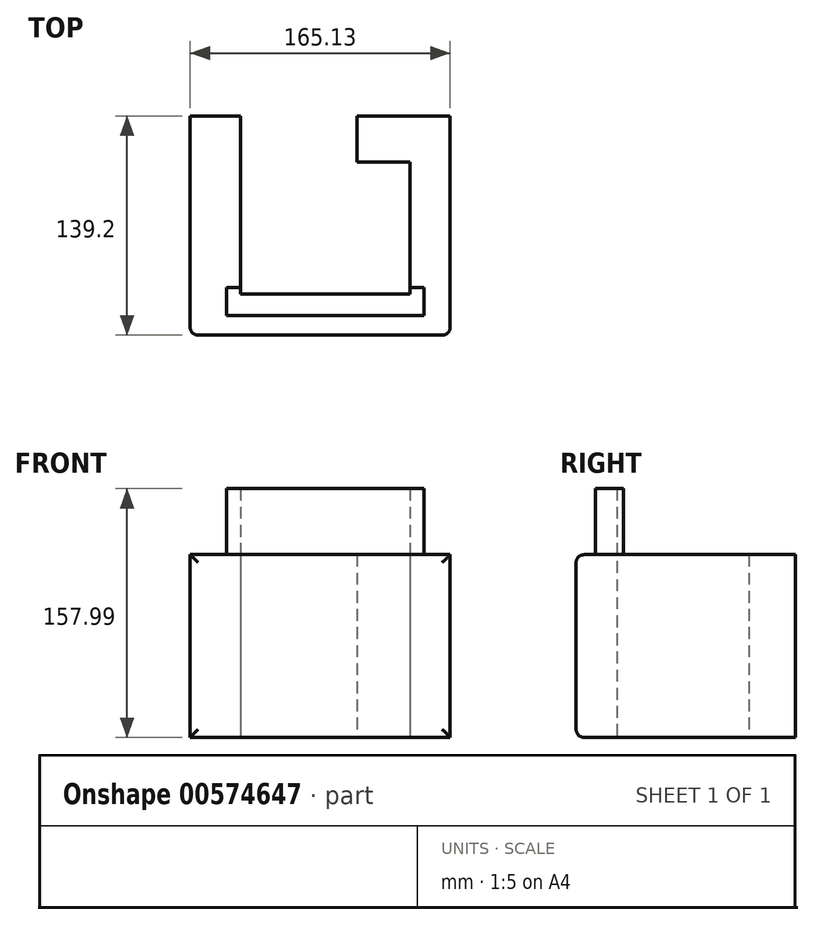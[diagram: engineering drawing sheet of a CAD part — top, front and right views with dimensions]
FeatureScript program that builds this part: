
annotation { "Feature Type Name" : "Feature", "Feature Type Description" : "" }
export const myFeature = defineFeature(function(context is Context, id is Id, definition is map)
    precondition{}
    {
        {
            var Q0;
            Q0=qCreatedBy(makeId("Top.planeOp"),FACE);
            var sketch = newSketch(context, id + "F0", { "sketchPlane" : qUnion([Q0])});
            skLineSegment(sketch, "E0", {"start": v(-79.65, 58) * mm, "end": v(-79.65, -81.2) * mm});
            skLineSegment(sketch, "E1", {"start": v(-79.65, -81.2) * mm, "end": v(85.48, -81.2) * mm});
            skLineSegment(sketch, "E2", {"start": v(85.48, -81.2) * mm, "end": v(85.48, 58) * mm});
            skLineSegment(sketch, "E3", {"start": v(85.48, 58) * mm, "end": v(26.2, 58) * mm});
            skLineSegment(sketch, "E4", {"start": v(26.2, 58) * mm, "end": v(26.2, 28.68) * mm});
            skLineSegment(sketch, "E5", {"start": v(26.2, 28.68) * mm, "end": v(60.08, 28.68) * mm});
            skLineSegment(sketch, "E6", {"start": v(60.08, 28.68) * mm, "end": v(60.08, -55.2) * mm});
            skLineSegment(sketch, "E7", {"start": v(60.08, -55.2) * mm, "end": v(-47.59, -55.2) * mm});
            skLineSegment(sketch, "E8", {"start": v(-47.59, -55.2) * mm, "end": v(-47.59, 58) * mm});
            skLineSegment(sketch, "E9", {"start": v(-47.59, 58) * mm, "end": v(-79.65, 58) * mm});
            skSolve(sketch);
        }
        {
            var Q0;
            Q0 = qSketchRegion(id + "F0", true);
            var Q1;
            Q1=makeQuery(id+"FirvQWOyVRMODnM_0.opThicken","CAP_FACE",FACE,{"disambiguationData":[OSD([makeQuery(id+"F0.imprint","IMPRINT",FACE,{"disambiguationData":[TD([[makeQuery(id+"F0.imprint","IMPRINT",EDGE,{"derivedFrom":sQuery(id+"F0.wireOp",EDGE,"E0")}),1.0]])]})])],"isStart":false});
            extrude(context, id + "F1", {"entities" : qUnion([Q0, Q1]), "depth" : 116.08 * mm, "offsetDistance" : 25.4 * mm});
        }
        {
            var Q0;
            Q0=makeQuery(id+"F1.opExtrude","CAP_FACE",FACE,{"disambiguationData":[OSD([sQuery(id+"F0.wireOp",EDGE,"E0"),sQuery(id+"F0.wireOp",EDGE,"E1"),sQuery(id+"F0.wireOp",EDGE,"E2"),sQuery(id+"F0.wireOp",EDGE,"E3"),sQuery(id+"F0.wireOp",EDGE,"E4"),sQuery(id+"F0.wireOp",EDGE,"E5"),sQuery(id+"F0.wireOp",EDGE,"E6"),sQuery(id+"F0.wireOp",EDGE,"E7"),sQuery(id+"F0.wireOp",EDGE,"E8"),sQuery(id+"F0.wireOp",EDGE,"E9")])],"isStart":false});
            var sketch = newSketch(context, id + "F2", { "sketchPlane" : qUnion([Q0])});
            skLineSegment(sketch, "E10", {"start": v(42.3, -68.82) * mm, "end": v(68.92, -68.82) * mm});
            skLineSegment(sketch, "E11", {"start": v(68.92, -68.82) * mm, "end": v(68.92, -51.04) * mm});
            skLineSegment(sketch, "E12", {"start": v(68.92, -51.04) * mm, "end": v(60.08, -51.04) * mm});
            skLineSegment(sketch, "E13", {"start": v(60.08, -51.04) * mm, "end": v(60.08, -55.2) * mm});
            skLineSegment(sketch, "E14", {"start": v(60.08, -55.2) * mm, "end": v(42.3, -55.2) * mm});
            skLineSegment(sketch, "E15", {"start": v(42.3, -55.2) * mm, "end": v(42.3, -68.82) * mm});
            skLineSegment(sketch, "E16.MirrorCS", {"start": v(-47.59, -51.04) * mm, "end": v(-47.59, -55.2) * mm});
            skLineSegment(sketch, "E17.MirrorCS", {"start": v(-29.81, -68.82) * mm, "end": v(-56.43, -68.82) * mm});
            skLineSegment(sketch, "E18.MirrorCS", {"start": v(-47.59, -55.2) * mm, "end": v(-29.81, -55.2) * mm});
            skLineSegment(sketch, "E19.MirrorCS", {"start": v(-56.43, -51.04) * mm, "end": v(-47.59, -51.04) * mm});
            skLineSegment(sketch, "E20.MirrorCS", {"start": v(-29.81, -55.2) * mm, "end": v(-29.81, -68.82) * mm});
            skLineSegment(sketch, "E21.MirrorCS", {"start": v(-56.43, -68.82) * mm, "end": v(-56.43, -51.04) * mm});
            skSolve(sketch);
        }
        {
            var Q0;
            Q0 = qSketchRegion(id + "F2", true);
            extrude(context, id + "F3", {"entities" : qUnion([Q0]), "operationType" : NewBodyOperationType.ADD, "depth" : 41.9 * mm, "offsetDistance" : 25.4 * mm});
        }
        {
            var Q0;
            Q0=makeQuery(id+"F1.opExtrude","SWEPT_EDGE",EDGE,{"disambiguationData":[OSD([sQuery(id+"F0.wireOp",EDGE,"E0"),sQuery(id+"F0.wireOp",EDGE,"E1")])]});
            var Q1;
            Q1=makeQuery(id+"F1.opExtrude","SWEPT_EDGE",EDGE,{"disambiguationData":[OSD([sQuery(id+"F0.wireOp",EDGE,"E1"),sQuery(id+"F0.wireOp",EDGE,"E2")])]});
            var Q2;
            Q2=makeQuery(id+"F1.opExtrude","CAP_EDGE",EDGE,{"disambiguationData":[OSD([sQuery(id+"F0.wireOp",EDGE,"E1")])],"isStart":false});
            var Q3;
            Q3=makeQuery(id+"F1.opExtrude","CAP_EDGE",EDGE,{"disambiguationData":[OSD([sQuery(id+"F0.wireOp",EDGE,"E1")])],"isStart":true});
            fillet(context, id + "F4", {"entities" : qUnion([Q0, Q1, Q2, Q3]), "radius" : 5.08 * mm, "tangentPropagation" : true, "allowEdgeOverflow" : false});
        }
        {
            var Q1;
            Q1=makeQuery(id+"F3.opExtrude","SWEPT_FACE",FACE,{"disambiguationData":[OSD([sQuery(id+"F2.wireOp",EDGE,"E20.MirrorCS")])]});
            var Q2;
            Q2=makeQuery(id+"F3.opExtrude","SWEPT_FACE",FACE,{"disambiguationData":[OSD([sQuery(id+"F2.wireOp",EDGE,"E15")])]});
            loft(context, id + "F5", {"operationType" : NewBodyOperationType.ADD, "sheetProfilesArray" : [{ "sheetProfileEntities" : qUnion([Q1]) }, { "sheetProfileEntities" : qUnion([Q2]) }]});
        }
        {
            var Q0;
            Q0=makeQuery(id+"F1.opExtrude","CAP_FACE",FACE,{"disambiguationData":[OSD([sQuery(id+"F0.wireOp",EDGE,"E0"),sQuery(id+"F0.wireOp",EDGE,"E1"),sQuery(id+"F0.wireOp",EDGE,"E2"),sQuery(id+"F0.wireOp",EDGE,"E3"),sQuery(id+"F0.wireOp",EDGE,"E4"),sQuery(id+"F0.wireOp",EDGE,"E5"),sQuery(id+"F0.wireOp",EDGE,"E6"),sQuery(id+"F0.wireOp",EDGE,"E7"),sQuery(id+"F0.wireOp",EDGE,"E8"),sQuery(id+"F0.wireOp",EDGE,"E9")])],"isStart":true});
            extrude(context, id + "F6", {"entities" : qUnion([Q0]), "operationType" : NewBodyOperationType.ADD, "oppositeDirection" : true, "depth" : 36.32 * mm, "offsetDistance" : 25.4 * mm});
        }
    });
